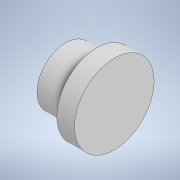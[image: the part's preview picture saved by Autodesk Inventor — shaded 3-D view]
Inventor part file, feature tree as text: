
AUTODESK INVENTOR PART (.ipt)
format: ipt  version: 2020 (Build 240168000, 168)  size: 113,664 bytes
history: native  units: in
note: dims shown in document units (in); Inventor stores cm internally (conversion verified against a paired STEP export)
features: extrude x2, sketch x2
ambient origin geometry x8: Origin, YZ Plane, XZ Plane, XY Plane, X Axis, Y Axis, Z Axis, Center Point
bodies: Solid1 (feature_tree)
feature tree (4):
  extrude  "Extrusion1"  Depth=0.1575in
  extrude  "Extrusion2"  Depth=0.2756in
  sketch  "Sketch1"  dims[d0=0.7087in d1=0.1575in]
  sketch  "Sketch2"  dims[d2=0.0in d3=0.5118in d4=0.2756in d5=0.0in]
